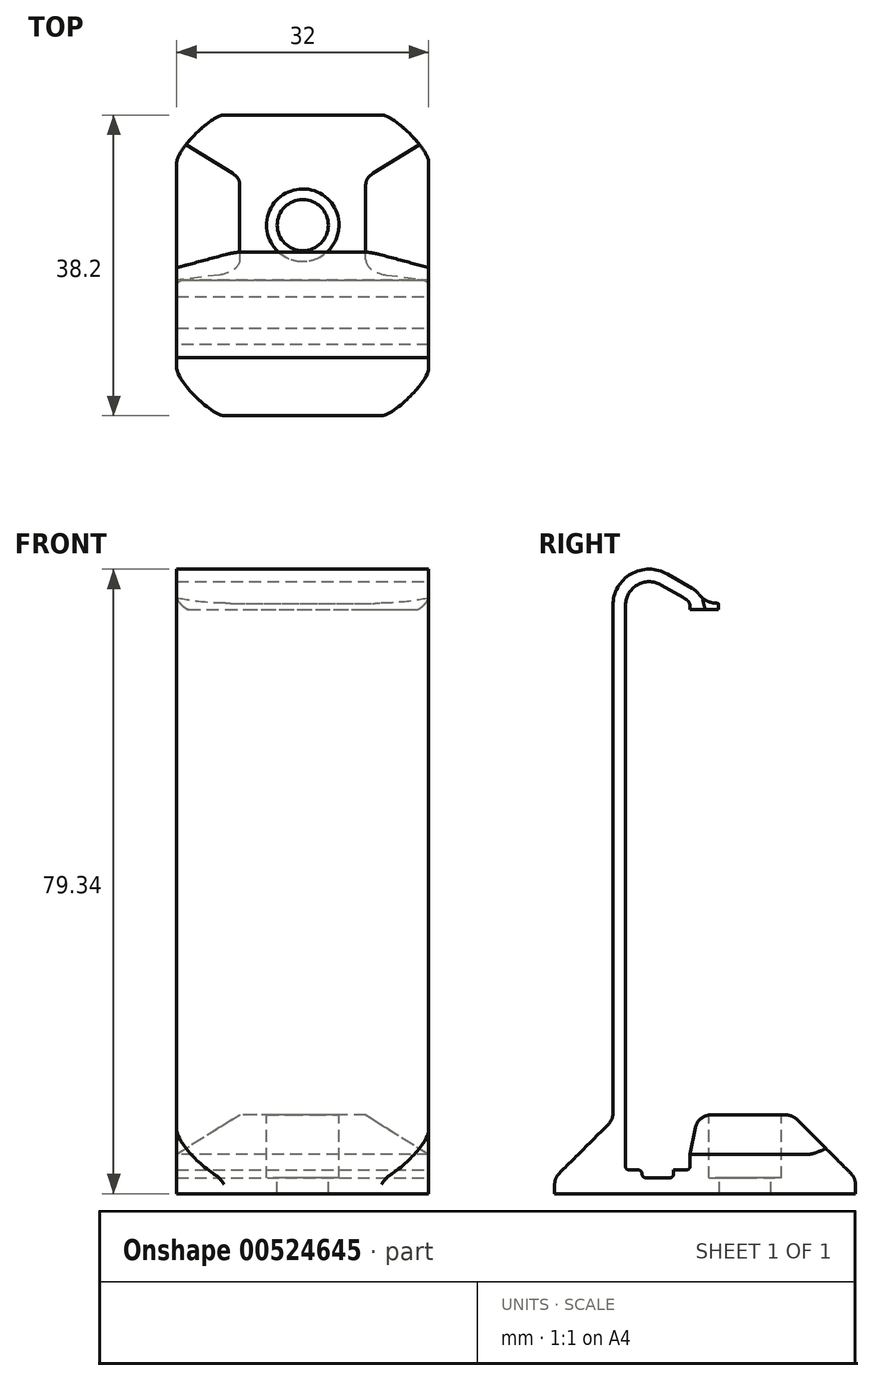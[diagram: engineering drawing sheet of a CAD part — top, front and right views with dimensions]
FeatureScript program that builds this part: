
annotation { "Feature Type Name" : "Feature", "Feature Type Description" : "" }
export const myFeature = defineFeature(function(context is Context, id is Id, definition is map)
    precondition{}
    {
        {
            var Q0;
            Q0=qCreatedBy(makeId("Right.planeOp"),FACE);
            var sketch = newSketch(context, id + "F0", { "sketchPlane" : qUnion([Q0])});
            skLineSegment(sketch, "E0.bottom", {"start": v(-4.1, 0) * mm, "end": v(4.1, 0) * mm});
            skLineSegment(sketch, "E0.top", {"start": v(-4.1, 72.2) * mm, "end": v(4.1, 72.2) * mm});
            skLineSegment(sketch, "E0.left", {"start": v(-4.1, 0) * mm, "end": v(-4.1, 72.2) * mm});
            skLineSegment(sketch, "E0.right", {"start": v(4.1, 0) * mm, "end": v(4.1, 72.2) * mm});
            skSolve(sketch);
        }
        {
            var Q0;
            Q0=qCreatedBy(makeId("Right.planeOp"),FACE);
            var sketch = newSketch(context, id + "F1", { "sketchPlane" : qUnion([Q0])});
            skLineSegment(sketch, "E1", {"start": v(-4.1, 6.4) * mm, "end": v(-5.7, 6.4) * mm});
            skLineSegment(sketch, "E2", {"start": v(-5.7, 6.4) * mm, "end": v(-13.1, -1) * mm});
            skLineSegment(sketch, "E3", {"start": v(-13.1, -1) * mm, "end": v(-13.1, -3) * mm});
            skLineSegment(sketch, "E4", {"start": v(-13.1, -3) * mm, "end": v(25.1, -3) * mm});
            skLineSegment(sketch, "E5", {"start": v(25.1, -3) * mm, "end": v(25.1, -1) * mm});
            skLineSegment(sketch, "E6", {"start": v(25.1, -1) * mm, "end": v(17.1, 7) * mm});
            skLineSegment(sketch, "E7", {"start": v(17.1, 7) * mm, "end": v(4.1, 7) * mm});
            skLineSegment(sketch, "E8", {"start": v(4.1, 7) * mm, "end": v(4.1, 0) * mm});
            skLineSegment(sketch, "E9", {"start": v(4.1, 0) * mm, "end": v(-4.1, 0) * mm});
            skLineSegment(sketch, "E10", {"start": v(-4.1, 0) * mm, "end": v(-4.1, 6.4) * mm});
            skSolve(sketch);
        }
        {
            var Q0;
            Q0=qSketchRegion(id+"F1",true);
            extrude(context, id + "F2", {"entities" : qUnion([Q0]), "endBound" : BoundingType.SYMMETRIC, "depth" : 32 * mm});
        }
        {
            var Q0;
            Q0=makeQuery(id+"F2.opExtrude","CAP_FACE",FACE,{"disambiguationData":[OSD([sQuery(id+"F1.wireOp",EDGE,"E1"),sQuery(id+"F1.wireOp",EDGE,"E2"),sQuery(id+"F1.wireOp",EDGE,"E3"),sQuery(id+"F1.wireOp",EDGE,"E4"),sQuery(id+"F1.wireOp",EDGE,"E5"),sQuery(id+"F1.wireOp",EDGE,"E6"),sQuery(id+"F1.wireOp",EDGE,"E7"),sQuery(id+"F1.wireOp",EDGE,"E8"),sQuery(id+"F1.wireOp",EDGE,"E9"),sQuery(id+"F1.wireOp",EDGE,"E10")])],"isStart":false});
            var sketch = newSketch(context, id + "F3", { "sketchPlane" : qUnion([Q0])});
            skLineSegment(sketch, "E11", {"start": v(-5.7, 6.4) * mm, "end": v(-4.1, 6.4) * mm});
            skLineSegment(sketch, "E12", {"start": v(-4.1, 6.4) * mm, "end": v(-4.1, 71.74) * mm});
            skLineSegment(sketch, "E13", {"start": v(0.4, 74.34) * mm, "end": v(3.6, 72.49) * mm});
            skLineSegment(sketch, "E14", {"start": v(4.1, 71.62) * mm, "end": v(4.1, 71.2) * mm});
            skLineSegment(sketch, "E15", {"start": v(4.1, 71.2) * mm, "end": v(5.7, 71.2) * mm});
            skLineSegment(sketch, "E16", {"start": v(5.7, 71.2) * mm, "end": v(5.7, 71.62) * mm});
            skLineSegment(sketch, "E17", {"start": v(4.4, 73.87) * mm, "end": v(1.2, 75.72) * mm});
            skLineSegment(sketch, "E18", {"start": v(-5.7, 71.74) * mm, "end": v(-5.7, 6.4) * mm});
            skArc(sketch, "E19", {"start": v(0.4, 74.34) * mm, "mid": v(-2.6, 74.34) * mm, "end": v(-4.1, 71.74) * mm});
            skArc(sketch, "E20", {"start": v(1.2, 75.72) * mm, "mid": v(-3.4, 75.72) * mm, "end": v(-5.7, 71.74) * mm});
            skArc(sketch, "E21", {"start": v(5.7, 71.62) * mm, "mid": v(5.35, 72.92) * mm, "end": v(4.4, 73.87) * mm});
            skArc(sketch, "E22", {"start": v(4.1, 71.62) * mm, "mid": v(3.97, 72.12) * mm, "end": v(3.6, 72.49) * mm});
            skLineSegment(sketch, "E23", {"start": v(3.6, 72.49) * mm, "end": v(4.1, 72.2) * mm, "construction": true});
            skLineSegment(sketch, "E24", {"start": v(4.1, 72.2) * mm, "end": v(4.1, 71.62) * mm, "construction": true});
            skLineSegment(sketch, "E25", {"start": v(4.1, 72.2) * mm, "end": v(-4.1, 71.74) * mm, "construction": true});
            skSolve(sketch);
        }
        {
            var Q0;
            Q0 = qSketchRegion(id + "F3", true);
            var Q1;
            Q1=makeQuery(id+"F2.opExtrude","CAP_FACE",FACE,{"disambiguationData":[OSD([sQuery(id+"F1.wireOp",EDGE,"E1"),sQuery(id+"F1.wireOp",EDGE,"E2"),sQuery(id+"F1.wireOp",EDGE,"E3"),sQuery(id+"F1.wireOp",EDGE,"E4"),sQuery(id+"F1.wireOp",EDGE,"E5"),sQuery(id+"F1.wireOp",EDGE,"E6"),sQuery(id+"F1.wireOp",EDGE,"E7"),sQuery(id+"F1.wireOp",EDGE,"E8"),sQuery(id+"F1.wireOp",EDGE,"E9"),sQuery(id+"F1.wireOp",EDGE,"E10")])],"isStart":true});
            extrude(context, id + "F4", {"entities" : qUnion([Q0]), "operationType" : NewBodyOperationType.ADD, "endBound" : BoundingType.UP_TO_SURFACE, "oppositeDirection" : true, "endBoundEntityFace" : qUnion([Q1]), "depth" : 25 * mm, "offsetDistance" : 25 * mm});
        }
        {
            var Q0;
            Q0=makeQuery(id+"F4.boolean.opBoolean","MERGE",FACE,{"derivedFrom":[makeQuery(id+"F2.opExtrude","CAP_FACE",FACE,{"disambiguationData":[OSD([sQuery(id+"F1.wireOp",EDGE,"E1"),sQuery(id+"F1.wireOp",EDGE,"E2"),sQuery(id+"F1.wireOp",EDGE,"E3"),sQuery(id+"F1.wireOp",EDGE,"E4"),sQuery(id+"F1.wireOp",EDGE,"E5"),sQuery(id+"F1.wireOp",EDGE,"E6"),sQuery(id+"F1.wireOp",EDGE,"E7"),sQuery(id+"F1.wireOp",EDGE,"E8"),sQuery(id+"F1.wireOp",EDGE,"E9"),sQuery(id+"F1.wireOp",EDGE,"E10")])],"isStart":false}),makeQuery(id+"F4.opExtrude","CAP_FACE",FACE,{"disambiguationData":[OSD([sQuery(id+"F3.wireOp",EDGE,"E11"),sQuery(id+"F3.wireOp",EDGE,"E12"),sQuery(id+"F3.wireOp",EDGE,"E13"),sQuery(id+"F3.wireOp",EDGE,"E14"),sQuery(id+"F3.wireOp",EDGE,"E15"),sQuery(id+"F3.wireOp",EDGE,"E16"),sQuery(id+"F3.wireOp",EDGE,"E17"),sQuery(id+"F3.wireOp",EDGE,"E18"),sQuery(id+"F3.wireOp",EDGE,"E19"),sQuery(id+"F3.wireOp",EDGE,"E20"),sQuery(id+"F3.wireOp",EDGE,"E21"),sQuery(id+"F3.wireOp",EDGE,"E22")])],"isStart":true})]});
            var sketch = newSketch(context, id + "F5", { "sketchPlane" : qUnion([Q0])});
            skLineSegment(sketch, "E26.bottom", {"start": v(-2, 0) * mm, "end": v(2, 0) * mm});
            skLineSegment(sketch, "E26.top", {"start": v(-2, -1) * mm, "end": v(2, -1) * mm});
            skLineSegment(sketch, "E26.left", {"start": v(-2, 0) * mm, "end": v(-2, -1) * mm});
            skLineSegment(sketch, "E26.right", {"start": v(2, 0) * mm, "end": v(2, -1) * mm});
            skLineSegment(sketch, "E27", {"start": v(-4.1, 0) * mm, "end": v(-2, 0) * mm});
            skLineSegment(sketch, "E28", {"start": v(2, 0) * mm, "end": v(4.1, 0) * mm});
            skSolve(sketch);
        }
        {
            var Q0;
            Q0=qSketchRegion(id+"F5",true);
            extrude(context, id + "F6", {"entities" : qUnion([Q0]), "operationType" : NewBodyOperationType.REMOVE, "endBound" : BoundingType.THROUGH_ALL, "oppositeDirection" : true, "depth" : 25 * mm});
        }
        {
            var Q0;
            Q0=makeQuery(id+"F2.opExtrude","SWEPT_EDGE",EDGE,{"disambiguationData":[OSD([sQuery(id+"F1.wireOp",EDGE,"E7"),sQuery(id+"F1.wireOp",EDGE,"E8")])]});
            chamfer(context, id + "F7", {"entities" : qUnion([Q0]), "chamferType" : ChamferType.TWO_OFFSETS, "width1" : 5 * mm, "oppositeDirection" : false, "width2" : 1 * mm, "tangentPropagation" : true});
        }
        {
            var Q0;
            Q0=makeQuery(id+"F2.opExtrude","SWEPT_FACE",FACE,{"disambiguationData":[OSD([sQuery(id+"F1.wireOp",EDGE,"E7")])]});
            var sketch = newSketch(context, id + "F8", { "sketchPlane" : qUnion([Q0])});
            skCircle(sketch, "E29", {"center": v(0, 11.1) * mm, "radius": 4.6 * mm});
            skLineSegment(sketch, "E30", {"start": v(0, 6.5) * mm, "end": v(0, 5.1) * mm, "construction": true});
            skLineSegment(sketch, "E31", {"start": v(0, 15.7) * mm, "end": v(0, 17.1) * mm, "construction": true});
            skSolve(sketch);
        }
        {
            var Q0;
            Q0=qSketchRegion(id+"F8",true);
            extrude(context, id + "F9", {"entities" : qUnion([Q0]), "operationType" : NewBodyOperationType.REMOVE, "oppositeDirection" : true, "depth" : 8 * mm});
        }
        {
            var Q0;
            Q0=makeQuery(id+"F9.boolean.opBoolean","COPY",FACE,{"derivedFrom":makeQuery(id+"F9.opExtrude","CAP_FACE",FACE,{"disambiguationData":[OSD([sQuery(id+"F8.wireOp",EDGE,"E29")])],"isStart":false})});
            var sketch = newSketch(context, id + "F10", { "sketchPlane" : qUnion([Q0])});
            skCircle(sketch, "E32", {"center": v(0, 11.1) * mm, "radius": 3.25 * mm});
            skSolve(sketch);
        }
        {
            var Q0;
            Q0=qSketchRegion(id+"F10",true);
            extrude(context, id + "F11", {"entities" : qUnion([Q0]), "operationType" : NewBodyOperationType.REMOVE, "endBound" : BoundingType.UP_TO_NEXT, "oppositeDirection" : true, "depth" : 25 * mm});
        }
        {
            var Q0;
            Q0=makeQuery(id+"F2.opExtrude","SWEPT_EDGE",EDGE,{"disambiguationData":[OSD([sQuery(id+"F1.wireOp",EDGE,"E9"),sQuery(id+"F1.wireOp",EDGE,"E10")])]});
            var Q1;
            Q1=makeQuery(id+"F2.opExtrude","SWEPT_EDGE",EDGE,{"disambiguationData":[OSD([sQuery(id+"F1.wireOp",EDGE,"E8"),sQuery(id+"F1.wireOp",EDGE,"E9")])]});
            var Q2;
            Q2=makeQuery(id+"F2.opExtrude","SWEPT_EDGE",EDGE,{"disambiguationData":[OSD([sQuery(id+"F1.wireOp",EDGE,"E7"),sQuery(id+"F1.wireOp",EDGE,"E8")])]});
            var Q3;
            Q3=makeQuery(id+"F6.boolean.opBoolean","COPY",EDGE,{"derivedFrom":makeQuery(id+"F6.opExtrude","SWEPT_EDGE",EDGE,{"disambiguationData":[OSD([sQuery(id+"F5.wireOp",EDGE,"E26.top"),sQuery(id+"F5.wireOp",EDGE,"E26.right")])]})});
            var Q4;
            Q4=makeQuery(id+"F6.boolean.opBoolean","COPY",EDGE,{"derivedFrom":makeQuery(id+"F6.opExtrude","SWEPT_EDGE",EDGE,{"disambiguationData":[OSD([sQuery(id+"F5.wireOp",EDGE,"E26.top"),sQuery(id+"F5.wireOp",EDGE,"E26.left")])]})});
            var Q5;
            Q5=makeQuery(id+"F6.boolean.opBoolean","COPY",EDGE,{"derivedFrom":makeQuery(id+"F6.opExtrude","SWEPT_EDGE",EDGE,{"disambiguationData":[OSD([sQuery(id+"F5.wireOp",EDGE,"E26.bottom"),sQuery(id+"F5.wireOp",EDGE,"E26.right"),sQuery(id+"F5.wireOp",EDGE,"E28")])]})});
            var Q6;
            Q6=makeQuery(id+"F6.boolean.opBoolean","COPY",EDGE,{"derivedFrom":makeQuery(id+"F6.opExtrude","SWEPT_EDGE",EDGE,{"disambiguationData":[OSD([sQuery(id+"F5.wireOp",EDGE,"E26.bottom"),sQuery(id+"F5.wireOp",EDGE,"E26.left"),sQuery(id+"F5.wireOp",EDGE,"E27")])]})});
            fillet(context, id + "F12", {"entities" : qUnion([Q0, Q1, Q2, Q3, Q4, Q5, Q6]), "radius" : .5 * mm, "tangentPropagation" : true, "allowEdgeOverflow" : false});
        }
        {
            var Q0;
            Q0=makeQuery(id+"F2.opExtrude","SWEPT_EDGE",EDGE,{"disambiguationData":[OSD([sQuery(id+"F1.wireOp",EDGE,"E5"),sQuery(id+"F1.wireOp",EDGE,"E6")])]});
            var Q1;
            Q1=makeQuery(id+"F2.opExtrude","SWEPT_EDGE",EDGE,{"disambiguationData":[OSD([sQuery(id+"F1.wireOp",EDGE,"E6"),sQuery(id+"F1.wireOp",EDGE,"E7")])]});
            var Q2;
            {var subQ0=sQuery(id+"F1.wireOp",EDGE,"E2");Q2=makeQuery(id+"F4.boolean.opBoolean","MERGE",EDGE,{"derivedFrom":[makeQuery(id+"F2.opExtrude","SWEPT_EDGE",EDGE,{"disambiguationData":[OSD([sQuery(id+"F1.wireOp",EDGE,"E1"),subQ0])]}),makeQuery(id+"F4.opExtrude","SWEPT_EDGE",EDGE,{"disambiguationData":[OSD([subQ0,sQuery(id+"F3.wireOp",EDGE,"E11"),sQuery(id+"F3.wireOp",EDGE,"E18")])]})]});}
            var Q3;
            Q3=makeQuery(id+"F2.opExtrude","SWEPT_EDGE",EDGE,{"disambiguationData":[OSD([sQuery(id+"F1.wireOp",EDGE,"E2"),sQuery(id+"F1.wireOp",EDGE,"E3")])]});
            var Q4;
            {var subQ0=sQuery(id+"F1.wireOp",EDGE,"E7");Q4=makeQuery(id+"F7.opChamfer","BLEND_EDGE",EDGE,{"blendedFrom":[makeQuery(id+"F2.opExtrude","SWEPT_EDGE",EDGE,{"disambiguationData":[OSD([subQ0,sQuery(id+"F1.wireOp",EDGE,"E8")])]}),makeQuery(id+"F2.opExtrude","SWEPT_FACE",FACE,{"disambiguationData":[OSD([subQ0])]})],"blendedInto":[makeQuery(id+"F2.opExtrude","SWEPT_FACE",FACE,{"disambiguationData":[OSD([subQ0])]})]});}
            fillet(context, id + "F13", {"entities" : qUnion([Q0, Q1, Q2, Q3, Q4]), "radius" : 2 * mm, "tangentPropagation" : true, "allowEdgeOverflow" : false});
        }
        {
            var Q0;
            Q0=makeQuery(id+"F2.opExtrude","CAP_EDGE",EDGE,{"disambiguationData":[OSD([sQuery(id+"F1.wireOp",EDGE,"E3")])],"isStart":false});
            var Q1;
            Q1=makeQuery(id+"F2.opExtrude","CAP_EDGE",EDGE,{"disambiguationData":[OSD([sQuery(id+"F1.wireOp",EDGE,"E5")])],"isStart":false});
            var Q2;
            Q2=makeQuery(id+"F2.opExtrude","CAP_EDGE",EDGE,{"disambiguationData":[OSD([sQuery(id+"F1.wireOp",EDGE,"E5")])],"isStart":true});
            var Q3;
            Q3=makeQuery(id+"F2.opExtrude","CAP_EDGE",EDGE,{"disambiguationData":[OSD([sQuery(id+"F1.wireOp",EDGE,"E3")])],"isStart":true});
            fillet(context, id + "F14", {"entities" : qUnion([Q0, Q1, Q2, Q3]), "radius" : 6 * mm, "rho" : .2, "crossSection" : FilletCrossSection.CONIC, "allowEdgeOverflow" : false});
        }
        {
            var Q0;
            Q0=makeQuery(id+"F2.opExtrude","CAP_EDGE",EDGE,{"disambiguationData":[OSD([sQuery(id+"F1.wireOp",EDGE,"E7")])],"isStart":true});
            var Q1;
            Q1=makeQuery(id+"F2.opExtrude","CAP_EDGE",EDGE,{"disambiguationData":[OSD([sQuery(id+"F1.wireOp",EDGE,"E7")])],"isStart":false});
            chamfer(context, id + "F15", {"entities" : qUnion([Q0, Q1]), "chamferType" : ChamferType.TWO_OFFSETS, "width1" : 8 * mm, "oppositeDirection" : false, "width2" : 5 * mm});
        }
        {
            var Q0;
            Q0=makeQuery(id+"F4.opExtrude","SWEPT_FACE",FACE,{"disambiguationData":[OSD([sQuery(id+"F3.wireOp",EDGE,"E15")])]});
            var sketch = newSketch(context, id + "F16", { "sketchPlane" : qUnion([Q0])});
            skLineSegment(sketch, "E33", {"start": v(-16, -5.7) * mm, "end": v(-9.8, -7.36) * mm});
            skLineSegment(sketch, "E34", {"start": v(-7.22, -7.7) * mm, "end": v(7.22, -7.7) * mm});
            skLineSegment(sketch, "E35", {"start": v(9.8, -7.36) * mm, "end": v(16, -5.7) * mm});
            skPoint(sketch, "E36.visualSharp", {"position": v(8.54, -7.7) * mm});
            skArc(sketch, "E36.filletArc", {"start": v(7.22, -7.7) * mm, "mid": v(8.52, -7.61) * mm, "end": v(9.8, -7.36) * mm});
            skPoint(sketch, "E37.visualSharp", {"position": v(-8.54, -7.7) * mm});
            skArc(sketch, "E37.filletArc", {"start": v(-9.8, -7.36) * mm, "mid": v(-8.52, -7.61) * mm, "end": v(-7.22, -7.7) * mm});
            skLineSegment(sketch, "E38", {"start": v(16, -5.7) * mm, "end": v(16, -4.1) * mm});
            skLineSegment(sketch, "E39", {"start": v(16, -4.1) * mm, "end": v(-16, -4.1) * mm});
            skLineSegment(sketch, "E40", {"start": v(-16, -4.1) * mm, "end": v(-16, -5.7) * mm});
            skSolve(sketch);
        }
        {
            var Q0;
            Q0=qSketchRegion(id+"F16",true);
            extrude(context, id + "F17", {"entities" : qUnion([Q0]), "operationType" : NewBodyOperationType.ADD, "oppositeDirection" : true, "depth" : .8 * mm});
        }
        {
            var Q0;
            Q0=makeQuery(id+"F17.boolean.opBoolean","INTERSECT",EDGE,{"derivedFrom":[makeQuery(id+"F4.opExtrude","SWEPT_FACE",FACE,{"disambiguationData":[OSD([sQuery(id+"F3.wireOp",EDGE,"E21")])]}),makeQuery(id+"F17.opExtrude","CAP_FACE",FACE,{"disambiguationData":[OSD([sQuery(id+"F16.wireOp",EDGE,"E33"),sQuery(id+"F16.wireOp",EDGE,"E34"),sQuery(id+"F16.wireOp",EDGE,"E35"),sQuery(id+"F16.wireOp",EDGE,"E36.filletArc"),sQuery(id+"F16.wireOp",EDGE,"E37.filletArc"),sQuery(id+"F16.wireOp",EDGE,"E38"),sQuery(id+"F16.wireOp",EDGE,"E39"),sQuery(id+"F16.wireOp",EDGE,"E40")])],"isStart":false})]});
            fillet(context, id + "F18", {"entities" : qUnion([Q0]), "radius" : 3 * mm, "tangentPropagation" : true, "allowEdgeOverflow" : false});
        }
        {
            var Q0;
            Q0=makeQuery(id+"F4.opExtrude","CAP_EDGE",EDGE,{"disambiguationData":[OSD([sQuery(id+"F3.wireOp",EDGE,"E15")])],"isStart":true});
            var Q1;
            Q1=makeQuery(id+"F4.opExtrude","CAP_EDGE",EDGE,{"disambiguationData":[OSD([sQuery(id+"F3.wireOp",EDGE,"E15")])],"isStart":false});
            fillet(context, id + "F19", {"entities" : qUnion([Q0, Q1]), "radius" : 1.5 * mm, "tangentPropagation" : true, "rho" : .2, "crossSection" : FilletCrossSection.CONIC, "allowEdgeOverflow" : false});
        }
    });
